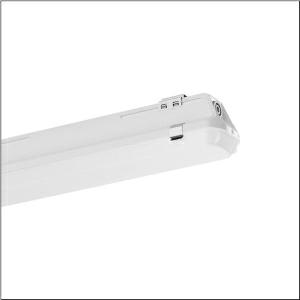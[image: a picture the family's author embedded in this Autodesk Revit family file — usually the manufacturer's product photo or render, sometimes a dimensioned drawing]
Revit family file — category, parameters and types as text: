
# Revit family: monsun_r__21_emergency_51fb10dp467b3h_4b81
name_source: partatom
category: Lighting Fixtures
units: mm (PartAtom-declared; Revit-internal decimal feet)

## family parameters
Cut with Voids When Loaded = No
Host = Face
Light Source = No
Part Type = Normal
Room Calculation Point = No
Round Connector Dimension = Use Diameter
Shared = No

## types (1)
- --- (1 x LED, 6060 lm, 42.2 W, 4000K)
    Apparent Load = 42 VA
    CIE Flux Codes = 47 77 93 94 100
    Color Rendering = 80
    Color Temperature = 4000K
    Default Elevation = 1800 mm
    Description = Monsun® 21 emergency, damp-proof luminaire, chain hanger, primary optical cover: enclosure, of PMMA, light emission: direct distribution, primary light characteristic: symmetric, installation type: vertical mounting, horizontal mounting, surface-mounted, suspended mounting, LED, rated luminous flux: 6.060lm, luminous efficacy: 144lm/W, light colour: 840, colour temperature: 4000K, control gear: ECG DALI, with terminal, 5+3-pole, max. 2.5mm², mains connection: 220..240V, AC, 50/60Hz, rated input power: 42W, control gear: single battery element, battery: NiCd, 4,5Ah, mains connection: 230V, housing, of glass-fibre reinforced polyester, uncoated, bright grey, incl. chain hanger, length: 1.590mm, width: 90mm, height: 88mm, clip for enclosure, of stainless steel (V2A), ceiling mounting element, of stainless steel (V2A), chain hanger, of stainless steel (V2A), protection rating (complete): IP66, insulation class (complete): insulation class I (protective earthing), certification: CE, UKCA, protection symbol: D, impact resistance: IK04, permissible operating ambient temperature: +5..+25°C, standard: EN 60598-2-1, EN 50419, EN 60598-2-22, corresponds to IFS (International Featured Standards) requirements for safety and quality in the food industry, for indoor or canopied outdoor use, no direct snow, no direct sun, no direct rain, contact your sales advisor before using the luminaires in applications with unclear chemical exposure, large temperature fluctuations or condensation-forming humidity, LABS conformity tested according to VDMA 24364:2018-05, packaging unit: 1 piece
    Height = 89 mm
    Lamp = 1 x LED
    Lamp Light Flux = 6060 lm
    Lamp Power = 42.2 W
    Lamp count = 1
    Length = 1590 mm
    Luminous efficacy = 144 lm/W
    Manufacturer = Siteco
    ModVariant = No
    Model = 51FB10DP467B3H
    Mounting Place = Ceiling
    Mounting Type = Surface mounted
    Number of Poles = 1
    OnlyDefault = Yes
    Power Factor = 1
    Product Name = Monsun® 21 emergency
    Product group = damp-proof luminaire
    ProductGroupID = 300
    Protection Class = Protection class I
    Protection Degree = IP 66
    RLX_Detail_Level = 1
    RLX_Emergency_Light_Flux = 0 lm
    RLX_Emergency_Type = 0
    RLX_Emergency_Type_DB = No
    RlxData = <blob elided: 92329 chars, md5=1c08c7ec>
    Socket = socket
    Standby Power = 0 W
    System Light Flux = 6060 lm
    System Power = 42 W
    Type Comments = factory setting: luminous flux: 100 % | dim-lin: 254 | 261 mA
    Type Image = l_1006717.jpg
    URL = http://relux.com
    VarID = @adj_134131
    Voltage = 0 V
    Weight = 0.00 kg
    Width = 90 mm

## geometry (parser evidence)
native form markers: Blend x4, Sweep x13
no freeform markers — native parametric forms only
